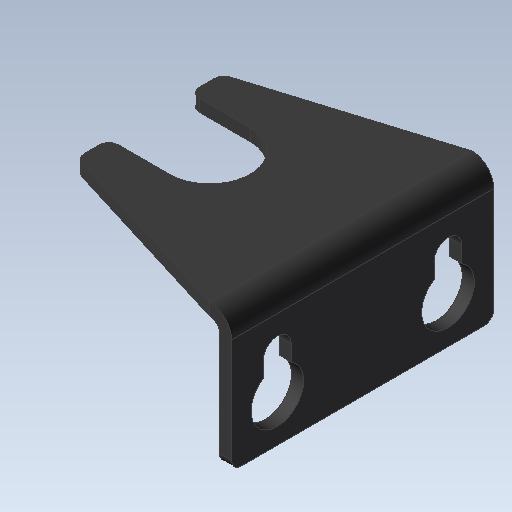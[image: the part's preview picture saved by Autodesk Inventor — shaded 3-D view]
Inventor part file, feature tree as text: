
AUTODESK INVENTOR PART (.ipt)
format: ipt  version: 2021.2 (Build 252289000, 289)  size: 131,584 bytes
history: native  units: in
note: dims shown in document units (in); Inventor stores cm internally (conversion verified against a paired STEP export)
features: fillet x1
ambient origin geometry x8: Origin, YZ Plane, XZ Plane, XY Plane, X Axis, Y Axis, Z Axis, Center Point
bodies: Solid1 (feature_tree)
feature tree (1):
  fillet  "Fillet1"  [1 undecoded]
note: 1 required parameter value undecoded (feature->parameter linkage not recoverable at this tier; creation-order binding heuristic only, values carry confidence <= 0.55)
